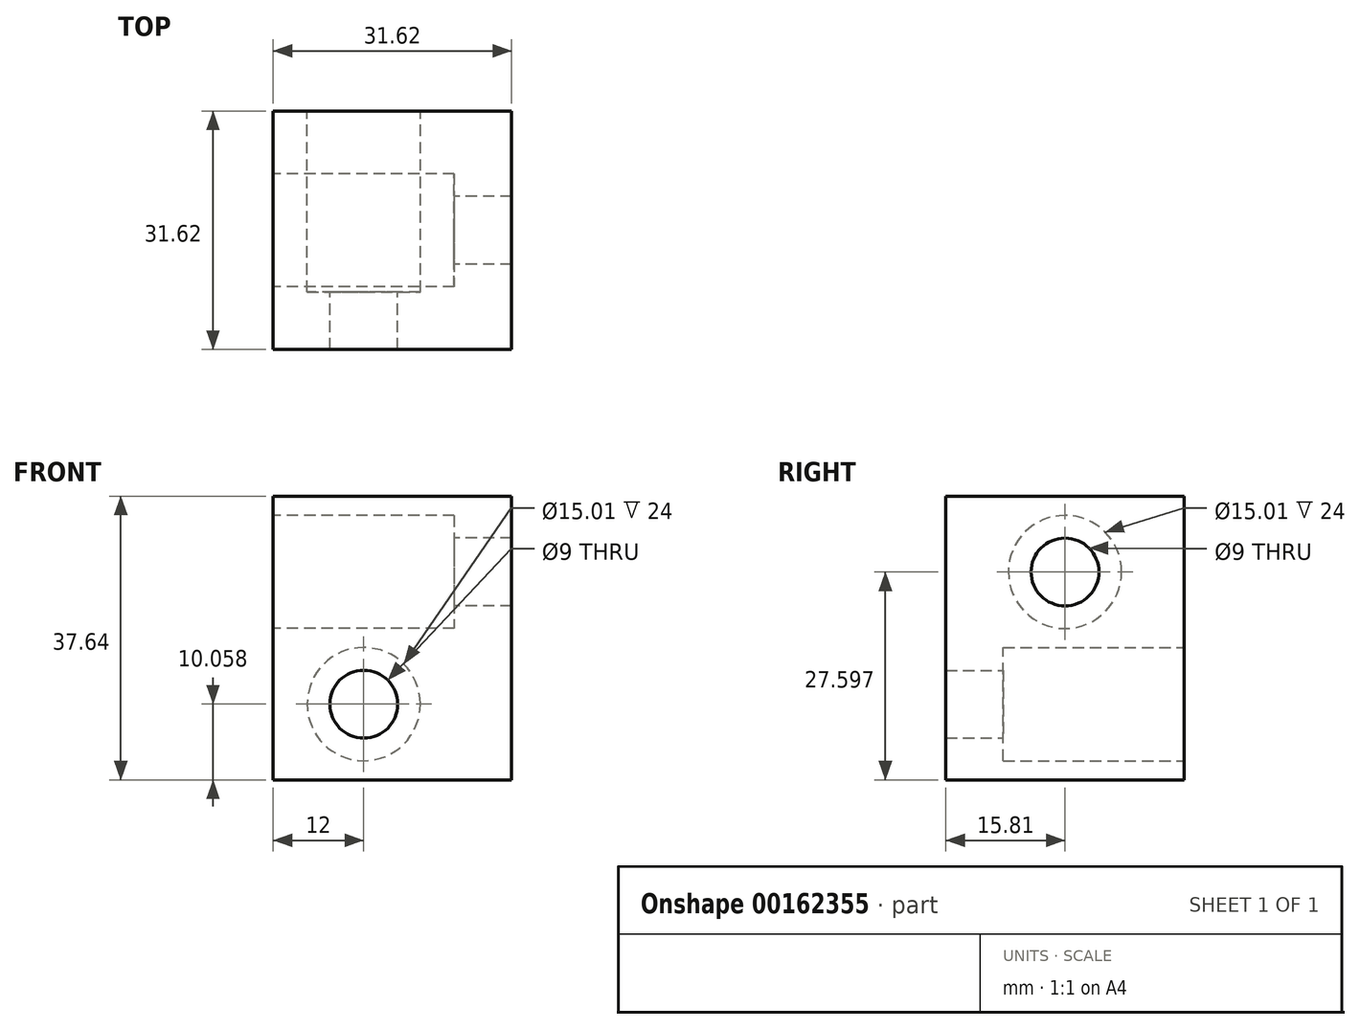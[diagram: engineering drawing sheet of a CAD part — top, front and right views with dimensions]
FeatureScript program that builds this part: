
annotation { "Feature Type Name" : "Feature", "Feature Type Description" : "" }
export const myFeature = defineFeature(function(context is Context, id is Id, definition is map)
    precondition{}
    {
        {
            var Q0;
            Q0=qCreatedBy(makeId("Front.planeOp"),FACE);
            var sketch = newSketch(context, id + "F0", { "sketchPlane" : qUnion([Q0])});
            skLineSegment(sketch, "E0.bottom", {"start": v(0, 0) * mm, "end": v(24, 0) * mm});
            skLineSegment(sketch, "E0.top", {"start": v(0, 37.64) * mm, "end": v(24, 37.64) * mm});
            skLineSegment(sketch, "E0.left", {"start": v(0, 0) * mm, "end": v(0, 37.64) * mm});
            skLineSegment(sketch, "E0.right", {"start": v(24, 0) * mm, "end": v(24, 37.64) * mm});
            skLineSegment(sketch, "E1", {"start": v(12, 0) * mm, "end": v(12, 37.64) * mm});
            skLineSegment(sketch, "E2", {"start": v(0, 10.06) * mm, "end": v(12, 10.06) * mm});
            skLineSegment(sketch, "E3", {"start": v(12, 10.06) * mm, "end": v(24, 10.06) * mm});
            skLineSegment(sketch, "E4", {"start": v(0, 27.58) * mm, "end": v(12, 27.58) * mm});
            skLineSegment(sketch, "E5", {"start": v(12, 27.58) * mm, "end": v(24, 27.58) * mm});
            skCircle(sketch, "E6", {"center": v(12, 10.06) * mm, "radius": 7.5 * mm});
            skSolve(sketch);
        }
        {
            var Q0;
            {var subQ1=sQuery(id+"F0.wireOp",EDGE,"E0.left");var subQ6=sQuery(id+"F0.wireOp",EDGE,"E0.bottom");var subQ9=makeQuery(id+"F0.imprint","INTERSECT",VERTEX,{"derivedFrom":[subQ6,subQ1]});Q0=makeQuery(id+"F0.imprint","IMPRINT",FACE,{"disambiguationData":[TD([[makeQuery(id+"F0.imprint","IMPRINT",EDGE,{"disambiguationData":[TD([[subQ9,-1.0]])],"derivedFrom":subQ6}),1.0]])]});}
            var Q1;
            {var subQ5=sQuery(id+"F0.wireOp",EDGE,"E4");Q1=makeQuery(id+"F0.imprint","IMPRINT",FACE,{"disambiguationData":[TD([[makeQuery(id+"F0.imprint","IMPRINT",EDGE,{"derivedFrom":subQ5}),-1.0]])]});}
            var Q2;
            {var subQ5=sQuery(id+"F0.wireOp",EDGE,"E4");Q2=makeQuery(id+"F0.imprint","IMPRINT",FACE,{"disambiguationData":[TD([[makeQuery(id+"F0.imprint","IMPRINT",EDGE,{"derivedFrom":subQ5}),1.0]])]});}
            var Q3;
            {var subQ5=sQuery(id+"F0.wireOp",EDGE,"E5");Q3=makeQuery(id+"F0.imprint","IMPRINT",FACE,{"disambiguationData":[TD([[makeQuery(id+"F0.imprint","IMPRINT",EDGE,{"derivedFrom":subQ5}),1.0]])]});}
            var Q4;
            {var subQ0=sQuery(id+"F0.wireOp",EDGE,"E5");Q4=makeQuery(id+"F0.imprint","IMPRINT",FACE,{"disambiguationData":[TD([[makeQuery(id+"F0.imprint","IMPRINT",EDGE,{"derivedFrom":subQ0}),-1.0]])]});}
            var Q5;
            {var subQ1=sQuery(id+"F0.wireOp",EDGE,"E0.bottom");var subQ5=sQuery(id+"F0.wireOp",EDGE,"E0.right");var subQ6=makeQuery(id+"F0.imprint","INTERSECT",VERTEX,{"derivedFrom":[subQ1,subQ5]});Q5=makeQuery(id+"F0.imprint","IMPRINT",FACE,{"disambiguationData":[TD([[makeQuery(id+"F0.imprint","IMPRINT",EDGE,{"disambiguationData":[TD([[subQ6,1.0]])],"derivedFrom":subQ1}),1.0]])]});}
            extrude(context, id + "F1", {"entities" : qUnion([Q0, Q1, Q2, Q3, Q4, Q5]), "depth" : 24 * mm});
        }
        {
            var Q0;
            Q0=makeQuery(id+"F1.opExtrude","SWEPT_FACE",FACE,{"disambiguationData":[OSD([sQuery(id+"F0.wireOp",EDGE,"E0.right")])]});
            var sketch = newSketch(context, id + "F2", { "sketchPlane" : qUnion([Q0])});
            skLineSegment(sketch, "E7.bottom", {"start": v(-24, 0) * mm, "end": v(0, 0) * mm});
            skLineSegment(sketch, "E7.top", {"start": v(-24, 37.64) * mm, "end": v(0, 37.64) * mm});
            skLineSegment(sketch, "E7.left", {"start": v(-24, 0) * mm, "end": v(-24, 37.64) * mm});
            skLineSegment(sketch, "E7.right", {"start": v(0, 0) * mm, "end": v(0, 37.64) * mm});
            skSolve(sketch);
        }
        {
            var Q0;
            Q0=makeQuery(id+"F2.imprint","IMPRINT",FACE,{"disambiguationData":[TD([[makeQuery(id+"F2.imprint","IMPRINT",EDGE,{"derivedFrom":sQuery(id+"F2.wireOp",EDGE,"E7.bottom")}),1.0]])]});
            var Q1;
            Q1=makeQuery(id+"F2.imprint","IMPRINT",FACE,{"disambiguationData":[TD([[makeQuery(id+"F2.imprint","IMPRINT",EDGE,{"derivedFrom":makeQuery(id+"Fr60UNIzFeQ3hM1_1.boolean.opBoolean","INTERSECT",EDGE,{"derivedFrom":[makeQuery(id+"F1.opExtrude","SWEPT_FACE",FACE,{"disambiguationData":[OSD([sQuery(id+"F0.wireOp",EDGE,"E0.right")])]}),makeQuery(id+"Fr60UNIzFeQ3hM1_1.opExtrude","SWEPT_FACE",FACE,{"disambiguationData":[OSD([sQuery(id+"FjbAwdkyWK0PSGg_1.wireOp",EDGE,"jjN5G9CZ-sFvP-OBZD-t7ju-oLrng3Lvo0sK")])]})]})}),-1.0]])]});
            extrude(context, id + "F3", {"entities" : qUnion([Q0, Q1]), "operationType" : NewBodyOperationType.ADD, "depth" : 7.62 * mm});
        }
        {
            var Q0;
            Q0=makeQuery(id+"F3.boolean.opBoolean","MERGE",FACE,{"derivedFrom":[makeQuery(id+"F1.opExtrude","CAP_FACE",FACE,{"disambiguationData":[OSD([sQuery(id+"F0.wireOp",EDGE,"E0.bottom"),sQuery(id+"F0.wireOp",EDGE,"E0.top"),sQuery(id+"F0.wireOp",EDGE,"E0.left"),sQuery(id+"F0.wireOp",EDGE,"E0.right"),sQuery(id+"F0.wireOp",EDGE,"E6")])],"isStart":false}),makeQuery(id+"F3.opExtrude","SWEPT_FACE",FACE,{"disambiguationData":[OSD([sQuery(id+"F2.wireOp",EDGE,"E7.left")])]})]});
            var sketch = newSketch(context, id + "F4", { "sketchPlane" : qUnion([Q0])});
            skLineSegment(sketch, "E8.bottom", {"start": v(0, 0) * mm, "end": v(31.62, 0) * mm});
            skLineSegment(sketch, "E8.top", {"start": v(0, 37.64) * mm, "end": v(31.62, 37.64) * mm});
            skLineSegment(sketch, "E8.left", {"start": v(0, 0) * mm, "end": v(0, 37.64) * mm});
            skLineSegment(sketch, "E8.right", {"start": v(31.62, 0) * mm, "end": v(31.62, 37.64) * mm});
            skSolve(sketch);
        }
        {
            var Q0;
            Q0=makeQuery(id+"F4.imprint","IMPRINT",FACE,{"disambiguationData":[TD([[makeQuery(id+"F4.imprint","IMPRINT",EDGE,{"derivedFrom":sQuery(id+"F4.wireOp",EDGE,"E8.bottom")}),1.0]])]});
            var Q1;
            Q1=makeQuery(id+"F4.imprint","IMPRINT",FACE,{"disambiguationData":[TD([[makeQuery(id+"F4.imprint","IMPRINT",EDGE,{"derivedFrom":makeQuery(id+"F1.opExtrude","CAP_EDGE",EDGE,{"disambiguationData":[OSD([sQuery(id+"F0.wireOp",EDGE,"E6")])],"isStart":false})}),1.0]])]});
            extrude(context, id + "F5", {"entities" : qUnion([Q0, Q1]), "operationType" : NewBodyOperationType.ADD, "depth" : 7.62 * mm});
        }
        {
            var Q0;
            Q0=makeQuery(id+"F5.opExtrude","CAP_FACE",FACE,{"disambiguationData":[OSD([sQuery(id+"F4.wireOp",EDGE,"E8.bottom"),sQuery(id+"F4.wireOp",EDGE,"E8.top"),sQuery(id+"F4.wireOp",EDGE,"E8.left"),sQuery(id+"F4.wireOp",EDGE,"E8.right")])],"isStart":true});
            var sketch = newSketch(context, id + "F6", { "sketchPlane" : qUnion([Q0])});
            skCircle(sketch, "E9", {"center": v(-12, 10.06) * mm, "radius": 4.5 * mm});
            skSolve(sketch);
        }
        {
            var Q0;
            Q0=makeQuery(id+"F6.imprint","IMPRINT",FACE,{"disambiguationData":[TD([[makeQuery(id+"F6.imprint","IMPRINT",EDGE,{"derivedFrom":sQuery(id+"F6.wireOp",EDGE,"E9")}),1.0]])]});
            extrude(context, id + "F7", {"entities" : qUnion([Q0]), "operationType" : NewBodyOperationType.REMOVE, "oppositeDirection" : true, "depth" : 25.4 * mm});
        }
        {
            var Q0;
            Q0=makeQuery(id+"F5.boolean.opBoolean","MERGE",FACE,{"derivedFrom":[makeQuery(id+"F1.opExtrude","SWEPT_FACE",FACE,{"disambiguationData":[OSD([sQuery(id+"F0.wireOp",EDGE,"E0.left")])]}),makeQuery(id+"F5.opExtrude","SWEPT_FACE",FACE,{"disambiguationData":[OSD([sQuery(id+"F4.wireOp",EDGE,"E8.left")])]})]});
            var sketch = newSketch(context, id + "F8", { "sketchPlane" : qUnion([Q0])});
            skCircle(sketch, "E10", {"center": v(15.81, 27.6) * mm, "radius": 7.5 * mm});
            skLineSegment(sketch, "E11", {"start": v(15.81, 27.6) * mm, "end": v(31.62, 27.6) * mm});
            skLineSegment(sketch, "E12", {"start": v(15.81, 27.6) * mm, "end": v(0, 27.6) * mm});
            skSolve(sketch);
        }
        {
            var Q0;
            {var subQ0=sQuery(id+"F8.wireOp",EDGE,"E11");var subQ1=sQuery(id+"F8.wireOp",EDGE,"E10");var subQ2=makeQuery(id+"F8.imprint","INTERSECT",VERTEX,{"derivedFrom":[subQ1,subQ0]});Q0=makeQuery(id+"F8.imprint","IMPRINT",FACE,{"disambiguationData":[TD([[makeQuery(id+"F8.imprint","IMPRINT",EDGE,{"disambiguationData":[TD([[subQ2,1.0]])],"derivedFrom":subQ1}),1.0]])]});}
            var Q1;
            {var subQ0=sQuery(id+"F8.wireOp",EDGE,"E11");var subQ1=sQuery(id+"F8.wireOp",EDGE,"E10");var subQ2=makeQuery(id+"F8.imprint","INTERSECT",VERTEX,{"derivedFrom":[subQ1,subQ0]});Q1=makeQuery(id+"F8.imprint","IMPRINT",FACE,{"disambiguationData":[TD([[makeQuery(id+"F8.imprint","IMPRINT",EDGE,{"disambiguationData":[TD([[subQ2,-1.0]])],"derivedFrom":subQ1}),1.0]])]});}
            extrude(context, id + "F9", {"entities" : qUnion([Q0, Q1]), "operationType" : NewBodyOperationType.REMOVE, "oppositeDirection" : true, "depth" : 24 * mm});
        }
        {
            var Q0;
            Q0=makeQuery(id+"F9.boolean.opBoolean","COPY",FACE,{"derivedFrom":makeQuery(id+"F9.opExtrude","CAP_FACE",FACE,{"disambiguationData":[OSD([sQuery(id+"F8.wireOp",EDGE,"E10")])],"isStart":false})});
            var sketch = newSketch(context, id + "F10", { "sketchPlane" : qUnion([Q0])});
            skCircle(sketch, "E13", {"center": v(15.81, 27.6) * mm, "radius": 4.5 * mm});
            skSolve(sketch);
        }
        {
            var Q0;
            Q0=makeQuery(id+"F10.imprint","IMPRINT",FACE,{"disambiguationData":[TD([[makeQuery(id+"F10.imprint","IMPRINT",EDGE,{"derivedFrom":sQuery(id+"F10.wireOp",EDGE,"E13")}),1.0]])]});
            extrude(context, id + "F11", {"entities" : qUnion([Q0]), "operationType" : NewBodyOperationType.REMOVE, "oppositeDirection" : true, "depth" : 25.4 * mm});
        }
    });
